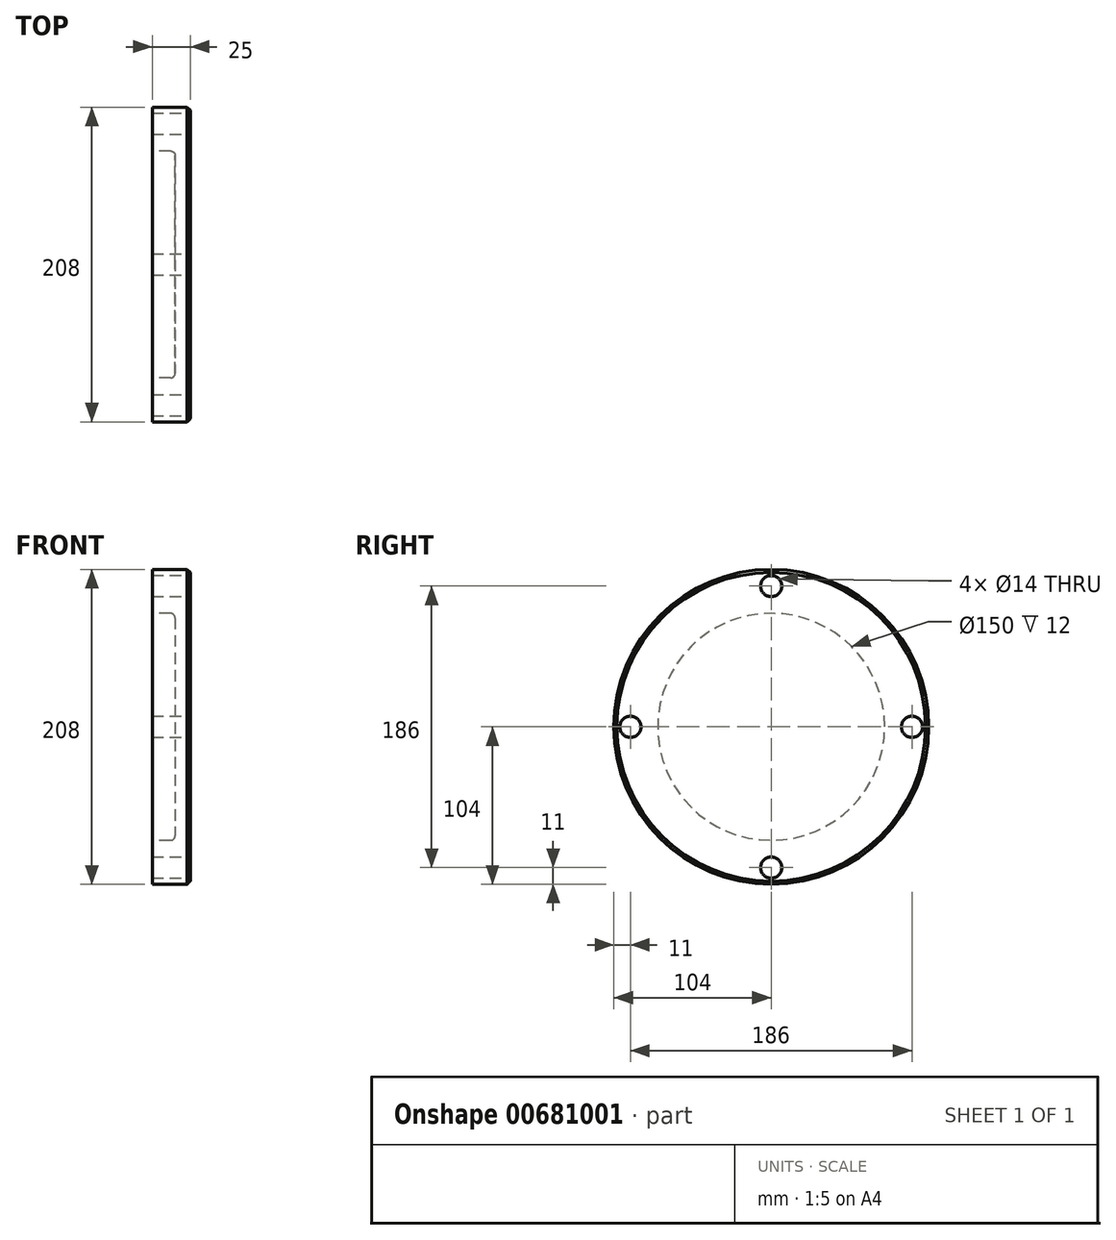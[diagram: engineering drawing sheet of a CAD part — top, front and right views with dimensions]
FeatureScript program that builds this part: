
annotation { "Feature Type Name" : "Feature", "Feature Type Description" : "" }
export const myFeature = defineFeature(function(context is Context, id is Id, definition is map)
    precondition{}
    {
        {
            var Q0;
            Q0=qCreatedBy(makeId("Right.planeOp"),FACE);
            var sketch = newSketch(context, id + "F0", { "sketchPlane" : qUnion([Q0])});
            skCircle(sketch, "E0", {"center": v(0, 0) * mm, "radius": 104 * mm});
            skSolve(sketch);
        }
        {
            var Q0;
            Q0=qSketchRegion(id+"F0",true);
            extrude(context, id + "F1", {"entities" : qUnion([Q0]), "oppositeDirection" : true, "depth" : 25 * mm, "offsetDistance" : 25 * mm});
        }
        {
            var Q0;
            Q0=makeQuery(id+"F1.opExtrude","CAP_FACE",FACE,{"disambiguationData":[OSD([sQuery(id+"F0.wireOp",EDGE,"E0")])],"isStart":false});
            var sketch = newSketch(context, id + "F2", { "sketchPlane" : qUnion([Q0])});
            skCircle(sketch, "E1", {"center": v(0, 0) * mm, "radius": 75 * mm});
            skSolve(sketch);
        }
        {
            var Q0;
            Q0=qSketchRegion(id+"F2",true);
            extrude(context, id + "F3", {"entities" : qUnion([Q0]), "operationType" : NewBodyOperationType.REMOVE, "oppositeDirection" : true, "depth" : 15 * mm, "offsetDistance" : 25 * mm});
        }
        {
            var Q0;
            Q0=makeQuery(id+"F3.boolean.opBoolean","COPY",EDGE,{"derivedFrom":makeQuery(id+"F3.opExtrude","CAP_EDGE",EDGE,{"disambiguationData":[OSD([sQuery(id+"F2.wireOp",EDGE,"E1")])],"isStart":false})});
            fillet(context, id + "F4", {"entities" : qUnion([Q0]), "radius" : 3 * mm, "tangentPropagation" : true, "allowEdgeOverflow" : false});
        }
        {
            var Q0;
            Q0=makeQuery(id+"F1.opExtrude","CAP_EDGE",EDGE,{"disambiguationData":[OSD([sQuery(id+"F0.wireOp",EDGE,"E0")])],"isStart":true});
            chamfer(context, id + "F5", {"entities" : qUnion([Q0]), "width" : 2 * mm, "tangentPropagation" : true});
        }
        {
            var Q0;
            Q0=makeQuery(id+"F1.opExtrude","CAP_FACE",FACE,{"disambiguationData":[OSD([sQuery(id+"F0.wireOp",EDGE,"E0")])],"isStart":true});
            var sketch = newSketch(context, id + "F6", { "sketchPlane" : qUnion([Q0])});
            skCircle(sketch, "E2", {"center": v(0, 0) * mm, "radius": 93 * mm, "construction": true});
            skLineSegment(sketch, "E3", {"start": v(0, 0) * mm, "end": v(0, 139.29) * mm, "construction": true});
            skPoint(sketch, "E4", {"position": v(0, 93) * mm});
            skPoint(sketch, "E5.1.0", {"position": v(-93, 0) * mm});
            skPoint(sketch, "E5.2.0", {"position": v(0, -93) * mm});
            skPoint(sketch, "E5.3.0", {"position": v(93, 0) * mm});
            skSolve(sketch);
        }
        {
            var Q0;
            Q0=sQuery(id+"F6.wireOp",VERTEX,"E4");
            var Q1;
            Q1=sQuery(id+"F6.wireOp",VERTEX,"E5.3.0");
            var Q2;
            Q2=sQuery(id+"F6.wireOp",VERTEX,"E5.2.0");
            var Q3;
            Q3=sQuery(id+"F6.wireOp",VERTEX,"E5.1.0");
            var Q4;
            Q4=makeQuery(id+"F1.opExtrude","SWEPT_BODY",BODY,{"disambiguationData":[OSD([sQuery(id+"F0.wireOp",EDGE,"E0")])]});
            hole(context, id + "F7", {"style" : HoleStyle.SIMPLE, "endStyle" : HoleEndStyle.THROUGH, "holeDiameter" : 14 * mm, "majorDiameter" : 5 * mm, "isTappedThrough" : true, "tappedDepth" : 24.75 * mm, "tapClearance" : 3, "locations" : qUnion([Q0, Q1, Q2, Q3]), "scope" : qUnion([Q4])});
        }
    });
